# Revit family: EKF_EE_КомплектКрепёжныхУголковДляМонтажнойПлатыTrivia_AVERES
name_source: partatom
category: Электрооборудование
units: mm (PartAtom-declared; Revit-internal decimal feet)

## family parameters
Всегда вертикально = Нет
На основе рабочей плоскости = Да
Общий = Да
При загрузке вырезать с полостями = Нет
Размер круглого соединителя = Использовать диаметр
Тип детали = Силовой щит
Точка расчета площади = Нет

## types (1)
- Комплект крепёжных уголков для монтажной платы (6 шт)  EKF AVERES
    ADSK_Единица измерения = шт.
    ADSK_Завод-изготовитель = EKF
    ADSK_Код изделия = AMPF6
    ADSK_Количество = 1
    ADSK_Марка = Комплект крепёжных уголков для монтажной платы (6 шт) EKF AVERES
    ADSK_Масса = 0
    ADSK_Материал = <По категории>
    ADSK_Наименование = Комплект крепёжных уголков для монтажной платы (6 шт) EKF AVERES
    ADSK_Обозначение = Комплект крепёжных уголков для монтажной платы (6 шт) EKF AVERES
    ADSK_Размер_Высота = 67 мм
    ADSK_Размер_Глубина = 37 мм
    ADSK_Размер_Ширина = 39 мм
    Изготовитель = EKF
    Отметка по умолчанию = 1219.2 мм
    Серия номенклатуры = Averes
    Степень защиты IP = -
    ТВ = EKF_2_TRIVIA_AVERES
    Тип = 655 мм
    Тип установки = -
